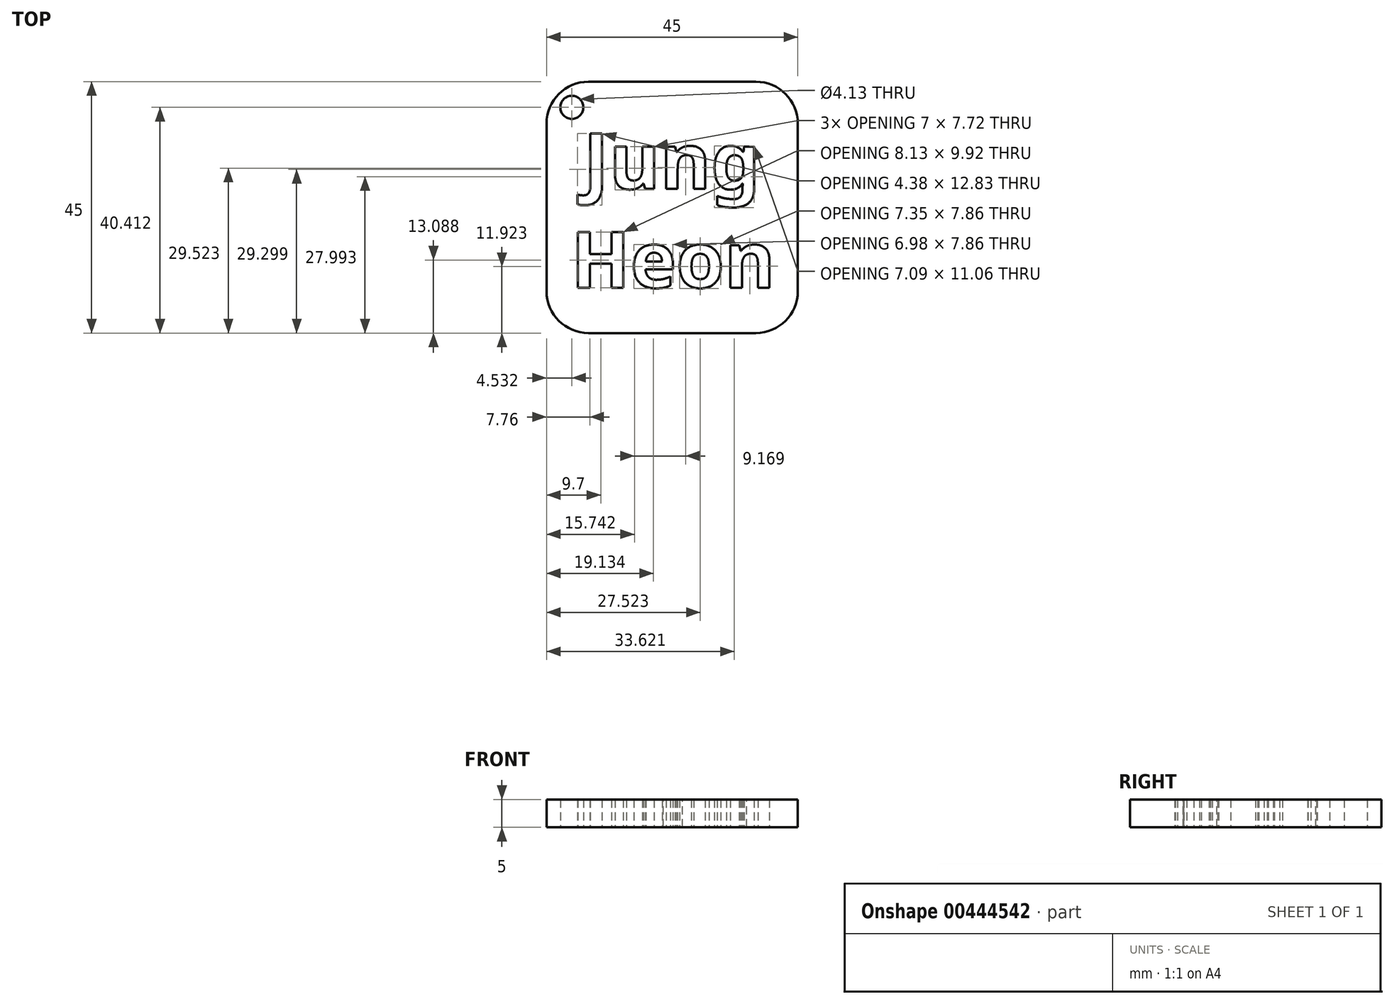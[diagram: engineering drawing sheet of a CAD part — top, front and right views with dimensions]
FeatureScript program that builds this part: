
annotation { "Feature Type Name" : "Feature", "Feature Type Description" : "" }
export const myFeature = defineFeature(function(context is Context, id is Id, definition is map)
    precondition{}
    {
        {
            var Q0;
            Q0=qCreatedBy(makeId("Top.planeOp"),FACE);
            var sketch = newSketch(context, id + "F0", { "sketchPlane" : qUnion([Q0])});
            skLineSegment(sketch, "E0.bottom", {"start": v(15, 22.5) * mm, "end": v(-15, 22.5) * mm});
            skLineSegment(sketch, "E0.top", {"start": v(15, -22.5) * mm, "end": v(-15, -22.5) * mm});
            skLineSegment(sketch, "E0.left", {"start": v(22.5, 15) * mm, "end": v(22.5, -15) * mm});
            skLineSegment(sketch, "E0.right", {"start": v(-22.5, 15) * mm, "end": v(-22.5, -15) * mm});
            skPoint(sketch, "E0.middle", {"position": v(0, 0) * mm});
            skPoint(sketch, "E1.visualSharp", {"position": v(-22.5, 22.5) * mm});
            skArc(sketch, "E1.filletArc", {"start": v(-15, 22.5) * mm, "mid": v(-20.3, 20.3) * mm, "end": v(-22.5, 15) * mm});
            skPoint(sketch, "E2.visualSharp", {"position": v(22.5, 22.5) * mm});
            skArc(sketch, "E2.filletArc", {"start": v(22.5, 15) * mm, "mid": v(20.3, 20.3) * mm, "end": v(15, 22.5) * mm});
            skPoint(sketch, "E3.visualSharp", {"position": v(22.5, -22.5) * mm});
            skArc(sketch, "E3.filletArc", {"start": v(15, -22.5) * mm, "mid": v(20.3, -20.3) * mm, "end": v(22.5, -15) * mm});
            skPoint(sketch, "E4.visualSharp", {"position": v(-22.5, -22.5) * mm});
            skArc(sketch, "E4.filletArc", {"start": v(-22.5, -15) * mm, "mid": v(-20.3, -20.3) * mm, "end": v(-15, -22.5) * mm});
            skSolve(sketch);
        }
        {
            var Q0;
            Q0 = qSketchRegion(id + "F0", true);
            extrude(context, id + "F1", {"entities" : qUnion([Q0]), "depth" : 5 * mm});
        }
        {
            var Q0;
            Q0=qCreatedBy(makeId("Top.planeOp"),FACE);
            var sketch = newSketch(context, id + "F2", { "sketchPlane" : qUnion([Q0])});
            skText(sketch, "E5", { "text": "Jung", "fontName": "NotoSans-Bold.ttf"});
            skText(sketch, "E6", { "text": "Heon", "fontName": "OpenSans-Bold.ttf"});
            skCircle(sketch, "E7", {"center": v(-17.97, 17.91) * mm, "radius": 2.07 * mm});
            const initialGuessF2  = {"E5": [-0.0159, 0.0033, 1, 0, 0.01], "E6": [-0.01811, -0.01437, 1, 0, 0.01]};
            skSetInitialGuess(sketch, initialGuessF2);
            skSolve(sketch);
        }
        {
            var Q0;
            Q0 = qSketchRegion(id + "F2", true);
            extrude(context, id + "F3", {"entities" : qUnion([Q0]), "operationType" : NewBodyOperationType.REMOVE, "depth" : 25 * mm});
        }
    });
